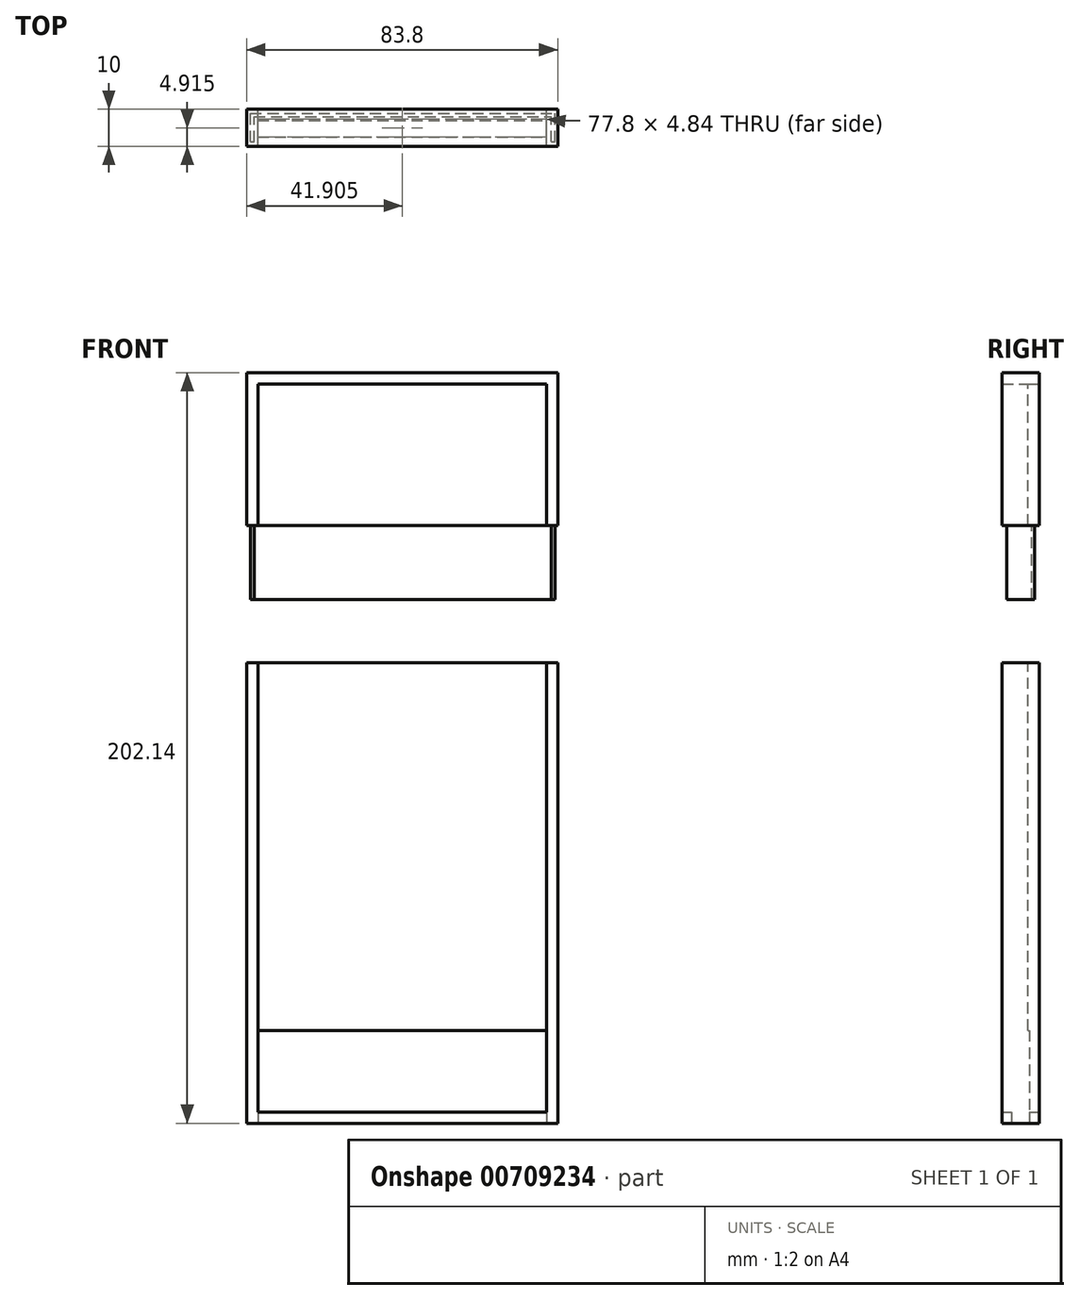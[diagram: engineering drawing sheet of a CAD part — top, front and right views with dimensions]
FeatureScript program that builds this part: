
annotation { "Feature Type Name" : "Feature", "Feature Type Description" : "" }
export const myFeature = defineFeature(function(context is Context, id is Id, definition is map)
    precondition{}
    {
        {
            var Q0;
            Q0=qCreatedBy(makeId("Front.planeOp"),FACE);
            var sketch = newSketch(context, id + "F0", { "sketchPlane" : qUnion([Q0])});
            skLineSegment(sketch, "E0.bottom", {"start": v(38.62, -60.5) * mm, "end": v(-39.18, -60.5) * mm});
            skLineSegment(sketch, "E0.left", {"start": v(38.62, -60.5) * mm, "end": v(38.62, 60.5) * mm});
            skLineSegment(sketch, "E0.right", {"start": v(-39.18, -60.5) * mm, "end": v(-39.18, 60.5) * mm});
            skPoint(sketch, "E0.middle", {"position": v(0, 0) * mm});
            skLineSegment(sketch, "E1.bottom", {"start": v(38.62, 97.54) * mm, "end": v(-39.18, 97.54) * mm});
            skLineSegment(sketch, "E1.top", {"start": v(38.62, 135.64) * mm, "end": v(-39.18, 135.64) * mm});
            skLineSegment(sketch, "E1.left", {"start": v(38.62, 97.54) * mm, "end": v(38.62, 135.64) * mm});
            skLineSegment(sketch, "E1.right", {"start": v(-39.18, 97.54) * mm, "end": v(-39.18, 135.64) * mm});
            skPoint(sketch, "E1.middle", {"position": v(-0.28, 118.09) * mm});
            skLineSegment(sketch, "E2.bottom", {"start": v(41.62, -63.5) * mm, "end": v(-42.18, -63.5) * mm});
            skLineSegment(sketch, "E2.left", {"start": v(41.62, -63.5) * mm, "end": v(41.62, 60.5) * mm});
            skLineSegment(sketch, "E2.right", {"start": v(-42.18, -63.5) * mm, "end": v(-42.18, 60.5) * mm});
            skPoint(sketch, "E2.middle", {"position": v(-0.28, -1.5) * mm});
            skLineSegment(sketch, "E3.bottom", {"start": v(41.62, 97.54) * mm, "end": v(-42.18, 97.54) * mm});
            skLineSegment(sketch, "E3.top", {"start": v(41.62, 138.64) * mm, "end": v(-42.18, 138.64) * mm});
            skLineSegment(sketch, "E3.left", {"start": v(41.62, 97.54) * mm, "end": v(41.62, 138.64) * mm});
            skLineSegment(sketch, "E3.right", {"start": v(-42.18, 97.54) * mm, "end": v(-42.18, 138.64) * mm});
            skLineSegment(sketch, "E4", {"start": v(-42.18, 60.5) * mm, "end": v(41.62, 60.5) * mm});
            skSolve(sketch);
        }
        {
            var Q0;
            Q0=makeQuery(id+"F0.imprint","IMPRINT",FACE,{"disambiguationData":[TD([[makeQuery(id+"F0.imprint","IMPRINT",EDGE,{"derivedFrom":sQuery(id+"F0.wireOp",EDGE,"E0.bottom")}),-1.0]])]});
            var Q1;
            Q1=makeQuery(id+"F0.imprint","IMPRINT",FACE,{"disambiguationData":[TD([[makeQuery(id+"F0.imprint","IMPRINT",EDGE,{"derivedFrom":sQuery(id+"F0.wireOp",EDGE,"E1.bottom")}),-1.0]])]});
            extrude(context, id + "F1", {"entities" : qUnion([Q0, Q1]), "depth" : 3 * mm, "offsetDistance" : 25 * mm});
        }
        {
            var Q0;
            Q0=makeQuery(id+"F0.imprint","IMPRINT",FACE,{"disambiguationData":[TD([[makeQuery(id+"F0.imprint","IMPRINT",EDGE,{"derivedFrom":sQuery(id+"F0.wireOp",EDGE,"E0.bottom")}),1.0]])]});
            var Q1;
            Q1=makeQuery(id+"F0.imprint","IMPRINT",FACE,{"disambiguationData":[TD([[makeQuery(id+"F0.imprint","IMPRINT",EDGE,{"derivedFrom":sQuery(id+"F0.wireOp",EDGE,"E1.top")}),-1.0]])]});
            extrude(context, id + "F2", {"entities" : qUnion([Q0, Q1]), "depth" : 10 * mm, "offsetDistance" : 25 * mm});
        }
        {
            var Q0;
            Q0=makeQuery(id+"F2.opExtrude","SWEPT_FACE",FACE,{"disambiguationData":[OSD([sQuery(id+"F0.wireOp",EDGE,"E2.bottom")])]});
            var sketch = newSketch(context, id + "F3", { "sketchPlane" : qUnion([Q0])});
            skLineSegment(sketch, "E5.bottom", {"start": v(-39.18, 7.5) * mm, "end": v(38.62, 7.5) * mm});
            skLineSegment(sketch, "E5.top", {"start": v(-39.18, 2.66) * mm, "end": v(38.62, 2.66) * mm});
            skLineSegment(sketch, "E5.left", {"start": v(-39.18, 7.5) * mm, "end": v(-39.18, 2.66) * mm});
            skLineSegment(sketch, "E5.right", {"start": v(38.62, 7.5) * mm, "end": v(38.62, 2.66) * mm});
            skSolve(sketch);
        }
        {
            var Q0;
            Q0=makeQuery(id+"F3.imprint","IMPRINT",FACE,{"disambiguationData":[TD([[makeQuery(id+"F3.imprint","IMPRINT",EDGE,{"derivedFrom":sQuery(id+"F3.wireOp",EDGE,"E5.bottom")}),-1.0]])]});
            extrude(context, id + "F4", {"entities" : qUnion([Q0]), "operationType" : NewBodyOperationType.REMOVE, "oppositeDirection" : true, "depth" : 25 * mm, "offsetDistance" : 25 * mm});
        }
        {
            var Q0;
            Q0=makeQuery(id+"F1.opExtrude","SWEPT_FACE",FACE,{"disambiguationData":[OSD([sQuery(id+"F0.wireOp",EDGE,"E1.bottom")])]});
            var sketch = newSketch(context, id + "F5", { "sketchPlane" : qUnion([Q0])});
            skLineSegment(sketch, "E6.bottom", {"start": v(-40.18, 2) * mm, "end": v(39.82, 2) * mm});
            skLineSegment(sketch, "E6.top", {"start": v(-39.18, 1.2) * mm, "end": v(39.82, 1.2) * mm});
            skLineSegment(sketch, "E7.bottom", {"start": v(-41.18, 8.8) * mm, "end": v(-40.18, 8.8) * mm});
            skLineSegment(sketch, "E7.left", {"start": v(-41.18, 8.8) * mm, "end": v(-41.18, 1.2) * mm});
            skLineSegment(sketch, "E7.right", {"start": v(-40.18, 8.8) * mm, "end": v(-40.18, 2) * mm});
            skLineSegment(sketch, "E8.bottom", {"start": v(39.82, 8.8) * mm, "end": v(40.82, 8.8) * mm});
            skLineSegment(sketch, "E8.top", {"start": v(39.82, 1.2) * mm, "end": v(40.82, 1.2) * mm});
            skLineSegment(sketch, "E8.left", {"start": v(39.82, 8.8) * mm, "end": v(39.82, 2) * mm});
            skLineSegment(sketch, "E8.right", {"start": v(40.82, 8.8) * mm, "end": v(40.82, 1.2) * mm});
            skLineSegment(sketch, "E9", {"start": v(-39.18, 2) * mm, "end": v(-39.18, 1.2) * mm});
            skLineSegment(sketch, "E10", {"start": v(38.62, 2) * mm, "end": v(38.62, 1.2) * mm});
            skLineSegment(sketch, "E11", {"start": v(-41.18, 1.2) * mm, "end": v(-39.18, 1.2) * mm});
            skSolve(sketch);
        }
        {
            var Q0;
            {var subQ0=sQuery(id+"F5.wireOp",EDGE,"E9");Q0=makeQuery(id+"F5.imprint","IMPRINT",FACE,{"disambiguationData":[TD([[makeQuery(id+"F5.imprint","IMPRINT",EDGE,{"derivedFrom":subQ0}),1.0]])]});}
            var Q1;
            Q1=makeQuery(id+"F5.imprint","IMPRINT",FACE,{"disambiguationData":[TD([[makeQuery(id+"F5.imprint","IMPRINT",EDGE,{"derivedFrom":sQuery(id+"F5.wireOp",EDGE,"E8.bottom")}),-1.0]])]});
            var Q2;
            Q2=makeQuery(id+"F5.imprint","IMPRINT",FACE,{"disambiguationData":[TD([[makeQuery(id+"F5.imprint","IMPRINT",EDGE,{"derivedFrom":sQuery(id+"F5.wireOp",EDGE,"E7.bottom")}),-1.0]])]});
            extrude(context, id + "F6", {"entities" : qUnion([Q0, Q1, Q2]), "depth" : 20 * mm, "offsetDistance" : 25 * mm});
        }
    });
